# Revit family: Legrand_Electric_vehicules_charging_stations_Green_up_Plastic_Connected_charging_stations
name_source: partatom
category: Equipement électrique
units: mm (PartAtom-declared; Revit-internal decimal feet)

## family parameters
Basée sur le plan de construction = Non
Configuration du panneau = Deux colonnes, circuits au sein
Cote de connecteur circulaire = Utiliser le diamètre
Couper avec des vides une fois chargée = Non
Numéro OmniClass = 23.80.30.11.17
Partagée = Non
Point de calcul de pièce = Non
Titre OmniClass = Distribution Boards and Control Panels
Toujours verticalement = Oui
Type d'élément = Tableau de raccordement

## types (10) — shared parameters
ETIM Class 6.0 = EC002883
Fabricant = Legrand
General Conditions of Use = https://export.legrand.com
Modèle = Green'up
Tension = 220
trigger safety signal transmission = 406276
zero-valued in all types: Elévation par défaut

## per-type parameters (varying)
| type | Description | Image du type | Puissance | URL | adjustment power | circuit breaker Protection line 2P+T (minimum) | circuit breaker diferential Protection line Type 2S | diferential | intensity Protection line 2P+T | intensity Protection line Type 2S | intensity terminal | section line 2P+T (minimum) | section line Type 2S (minimum) | terminal fixing wall | terminal in place |
| Single-phase Premium Green 'up wall mount Plastic - Mode 3 - 3,7/4,6kW - 16/20A | 059000  Single-phase Premium Green 'up wall mount Plastic - Mode 3 - 3,7/4,6kW - 16/20A | Borne_ve_plastique_murale_059000.jpg | 4.6 | www.legrand.fr | 4600 W |  | 410755 (4500/6 kA) | 30 mA type F (ex Hpi) |  | 20 A curve C | 20 A | 0 mm  [stored 0 ft] | 4 mm  [stored 0.0131234 ft] | Oui | Non |
| Single-phase Premium Green 'up wall mount Plastic - Modes 2 and 3 - 3,7/4,6kW - 16/20A | 059003  Single-phase Premium Green 'up wall mount Plastic - Modes 2 and 3 - 3,7/4,6kW - 16/20A | Borne_ve_plastique_murale_059000.jpg | 3.7 | www.legrand.fr | 4600 W | 406884 (4500/6kA) | 410755 (4500/6 kA) | 30 mA type F (ex Hpi) | 20 A curve C | 25 A curve C | 20 A | 3 mm  [stored 0.00984252 ft] | 4 mm  [stored 0.0131234 ft] | Oui | Non |
| Single-phase Premium Green 'up wall mount Plastic - Modes 2 and 3 - 7,4kW - 32A | 059004  Single-phase Premium Green 'up wall mount Plastic - Modes 2 and 3 - 7,4kW - 32A | Borne_ve_plastique_murale_059000.jpg | 3.7 | www.legrand.fr | 7400 W | 406884 (4500/6kA) | 410859 (4500/6 kA) | 30 mA type F (ex Hpi) | 20 A curve C | 40 A curve C | 32 A | 3 mm  [stored 0.00984252 ft] | 10 mm  [stored 0.0328084 ft] | Oui | Non |
| Single-phase Premium Green 'up Plastic - Mode 3 - 3,7/4,6kW - 16/20A | 059000 + 059052  Single-phase Premium Green 'up Plastic - Mode 3 - 3,7/4,6kW - 16/20A | Boren_ve_pied_059003_059052.png | 3.7 | www.legrand.fr | 3700 W |  | 410754 (4500/6 kA) | 30 mA type F (ex Hpi) |  | 20 A curve C | 16 A | 0 mm  [stored 0 ft] | 3 mm  [stored 0.00984252 ft] | Non | Oui |
| Single-phase Premium Green 'up Plastic - Modes 2 and 3 - 3,7/4,6kW - 16/20A | 059003 + 059052  Single-phase Premium Green 'up Plastic - Modes 2 and 3 - 3,7/4,6kW - 16/20A | Boren_ve_pied_059003_059052.png | 3.7 | www.legrand.Fr | 3700 W |  | 410754 (4500/6 kA) | 30 mA type F (ex Hpi) |  | 20 A curve C | 16 A | 0 mm  [stored 0 ft] | 3 mm  [stored 0.00984252 ft] | Non | Oui |
| Single-phase Premium Green 'up Plastic - Modes 2 and 3 - 7,4kW - 32A | 059004 + 059052  Single-phase Premium Green 'up Plastic - Modes 2 and 3 - 7,4kW - 32A | Boren_ve_pied_059003_059052.png | 3.7 | www.legrand.fr | 7400 W | 406884 (4500/6kA) | 410859 (4500/6 kA) | 30 mA type F (ex Hpi) |  | 20 A curve C | 32 A | 3 mm  [stored 0.00984252 ft] | 10 mm  [stored 0.0328084 ft] | Non | Oui |
| Single-phase Premium Green 'up wall mount Plastic - Mode 3 - 7,4kW - 32A | 059001  Single-phase Premium Green 'up wall mount Plastic - Mode 3 - 7,4kW - 32A | Borne_ve_plastique_murale_059000.jpg | 7.4 | www.legrand.fr | 7400 W |  | 410759 (6000/10 kA) | 30 mA type F (ex Hpi) |  | 40 A curve C | 32 A | 0 mm  [stored 0 ft] | 10 mm  [stored 0.0328084 ft] | Oui | Non |
| Single-phase Premium Green 'up Plastic - Mode 3 - 7,4kW - 32A | 059001 + 059052  Single-phase Premium Green 'up Plastic - Mode 3 - 7,4kW - 32A | Borne_ve_plastique_murale_059000.jpg | 7.4 | www.legrand.fr | 7400 W |  | 410759 (6000/10 kA) | 30 mA type F (ex Hpi) |  | 40 A curve C | 32 A | 0 mm  [stored 0 ft] | 10 mm  [stored 0.0328084 ft] | Non | Oui |
| Single-phase Premium Green 'up Plastic - Mode 3 - 22kW - 32A | 059002 + 059052  Single-phase Premium Green 'up Plastic - Mode 3 - 22kW - 32A | Boren_ve_pied_059003_059052.png | 22 | www.legrand.fr | 22000 W | 406884 (4500/6 kA) | 407902 (6000/10 kA) | 30 mA type B |  | 20 A curve C | 32 A | 3 mm  [stored 0.00984252 ft] | 10 mm  [stored 0.0328084 ft] | Non | Oui |
| Single-phase Premium Green 'up wall mount Plastic - Mode 3 - 22kW - 32A | 059002  Single-phase Premium Green 'up wall mount Plastic - Mode 3 - 22kW - 32A | Borne_ve_plastique_murale_059000.jpg | 22 | www.legrand.fr | 22000 W | 406884 (4500/6 kA) | 407902 (6000/10 kA) | 30 mA type B |  | 20 A curve C | 32 A | 3 mm  [stored 0.00984252 ft] | 10 mm  [stored 0.0328084 ft] | Oui | Non |

note: [stored X ft] marks values corroborated as IEEE doubles in the binary element streams (Revit-internal decimal feet)
